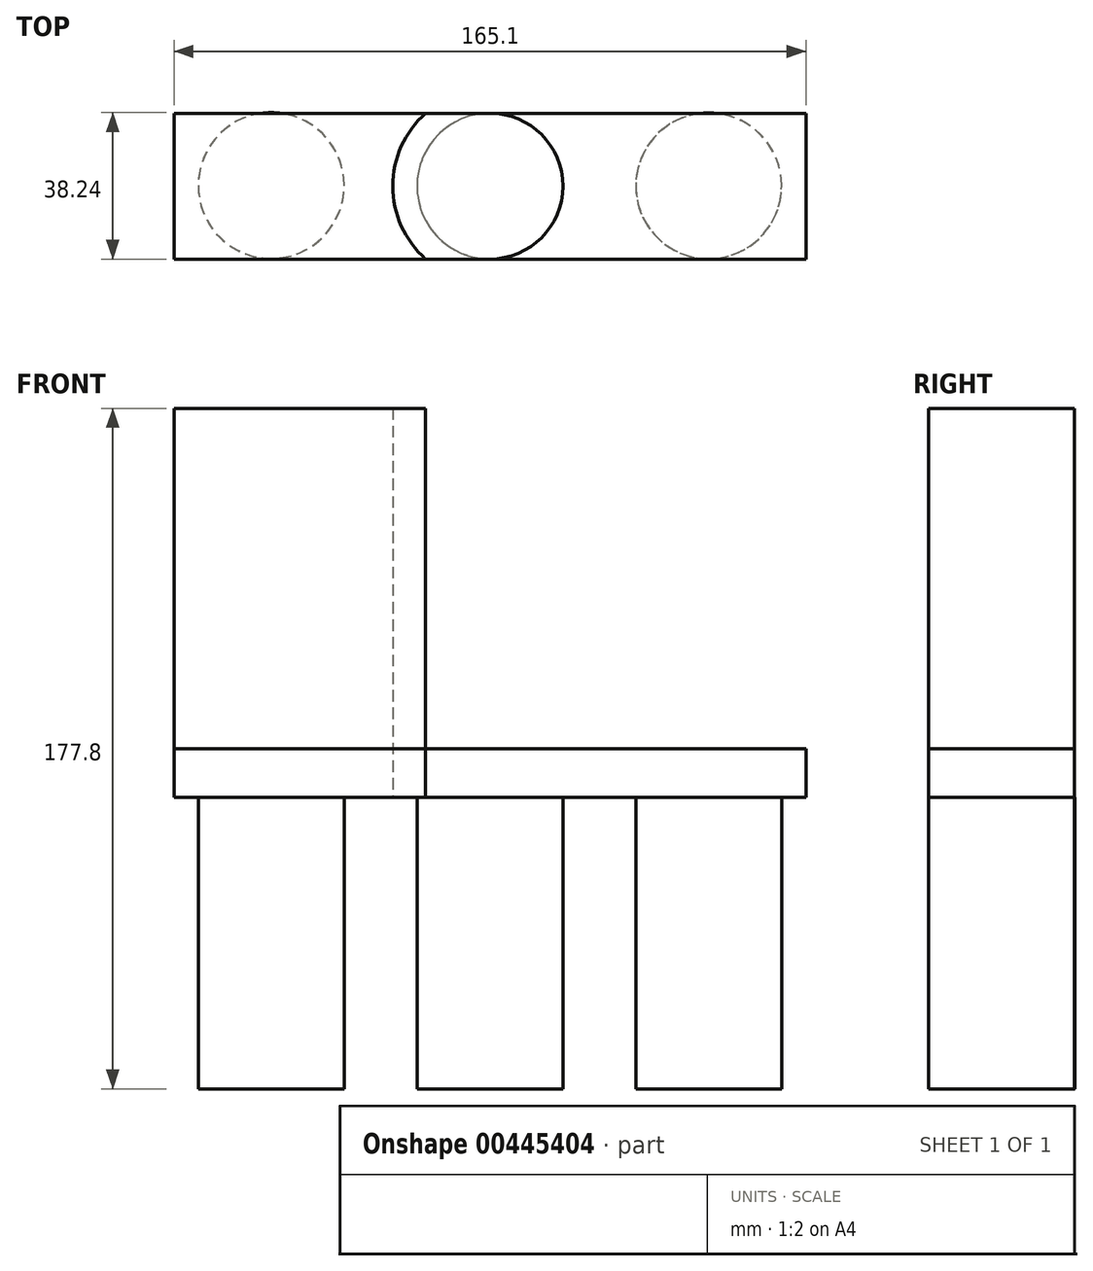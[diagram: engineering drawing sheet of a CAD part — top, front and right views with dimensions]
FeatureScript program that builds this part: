
annotation { "Feature Type Name" : "Feature", "Feature Type Description" : "" }
export const myFeature = defineFeature(function(context is Context, id is Id, definition is map)
    precondition{}
    {
        {
            var Q0;
            Q0=qCreatedBy(makeId("Top.planeOp"),FACE);
            var sketch = newSketch(context, id + "F0", { "sketchPlane" : qUnion([Q0])});
            skLineSegment(sketch, "E0.bottom", {"start": v(82.55, -19.05) * mm, "end": v(-82.55, -19.05) * mm});
            skLineSegment(sketch, "E0.top", {"start": v(82.55, 19.05) * mm, "end": v(-82.55, 19.05) * mm});
            skLineSegment(sketch, "E0.left", {"start": v(82.55, -19.05) * mm, "end": v(82.55, 19.05) * mm});
            skLineSegment(sketch, "E0.right", {"start": v(-82.55, -19.05) * mm, "end": v(-82.55, 19.05) * mm});
            skPoint(sketch, "E0.middle", {"position": v(0, 0) * mm});
            skCircle(sketch, "E1", {"center": v(0, 0) * mm, "radius": 25.4 * mm});
            skSolve(sketch);
        }
        {
            var Q0;
            Q0=makeQuery(id+"F0.imprint","IMPRINT",FACE,{"disambiguationData":[TD([[makeQuery(id+"F0.imprint","IMPRINT",EDGE,{"derivedFrom":sQuery(id+"F0.wireOp",EDGE,"E0.bottom")}),-1.0]])]});
            extrude(context, id + "F1", {"entities" : qUnion([Q0]), "depth" : 12.7 * mm});
        }
        {
            var Q0;
            {var subQ0=sQuery(id+"F0.wireOp",EDGE,"E1");var subQ1=sQuery(id+"F0.wireOp",EDGE,"E0.bottom");var subQ2=makeQuery(id+"F0.imprint","INTERSECT",VERTEX,{"disambiguationData":[OD(0.0)],"derivedFrom":[subQ1,subQ0]});Q0=makeQuery(id+"F0.imprint","IMPRINT",FACE,{"disambiguationData":[TD([[makeQuery(id+"F0.imprint","IMPRINT",EDGE,{"disambiguationData":[TD([[subQ2,-1.0]])],"derivedFrom":subQ1}),-1.0]])]});}
            var Q1;
            {var subQ0=sQuery(id+"F0.wireOp",EDGE,"E1");var subQ1=sQuery(id+"F0.wireOp",EDGE,"E0.top");var subQ2=makeQuery(id+"F0.imprint","INTERSECT",VERTEX,{"disambiguationData":[OD(0.0)],"derivedFrom":[subQ1,subQ0]});Q1=makeQuery(id+"F0.imprint","IMPRINT",FACE,{"disambiguationData":[TD([[makeQuery(id+"F0.imprint","IMPRINT",EDGE,{"disambiguationData":[TD([[subQ2,-1.0]])],"derivedFrom":subQ1}),-1.0]])]});}
            var Q2;
            {var subQ0=sQuery(id+"F0.wireOp",EDGE,"E1");var subQ1=sQuery(id+"F0.wireOp",EDGE,"E0.bottom");var subQ2=makeQuery(id+"F0.imprint","INTERSECT",VERTEX,{"disambiguationData":[OD(0.0)],"derivedFrom":[subQ1,subQ0]});Q2=makeQuery(id+"F0.imprint","IMPRINT",FACE,{"disambiguationData":[TD([[makeQuery(id+"F0.imprint","IMPRINT",EDGE,{"disambiguationData":[TD([[subQ2,-1.0]])],"derivedFrom":subQ1}),1.0]])]});}
            extrude(context, id + "F2", {"entities" : qUnion([Q0, Q1, Q2]), "depth" : 101.6 * mm});
        }
        {
            var Q0;
            Q0=qCreatedBy(makeId("Top.planeOp"),FACE);
            var sketch = newSketch(context, id + "F3", { "sketchPlane" : qUnion([Q0])});
            skCircle(sketch, "E2", {"center": v(0, 0) * mm, "radius": 19.05 * mm});
            skLineSegment(sketch, "E3", {"start": v(0, 0) * mm, "end": v(38.1, 0) * mm});
            skLineSegment(sketch, "E4", {"start": v(0, 0) * mm, "end": v(-38.1, 0) * mm});
            skCircle(sketch, "E5", {"center": v(-57.15, 0.14) * mm, "radius": 19.05 * mm});
            skPoint(sketch, "E5.second.point", {"position": v(-51.83, 18.43) * mm});
            skPoint(sketch, "E5.third.point", {"position": v(-76.2, 0) * mm});
            skCircle(sketch, "E6", {"center": v(57.15, 0.06) * mm, "radius": 19.05 * mm});
            skPoint(sketch, "E6.second.point", {"position": v(76.2, 0) * mm});
            skPoint(sketch, "E6.third.point", {"position": v(60.73, 18.77) * mm});
            skSolve(sketch);
        }
        {
            var Q0;
            Q0=makeQuery(id+"F3.imprint","IMPRINT",FACE,{"disambiguationData":[TD([[makeQuery(id+"F3.imprint","IMPRINT",EDGE,{"derivedFrom":sQuery(id+"F3.wireOp",EDGE,"E5")}),1.0]])]});
            var Q1;
            {var subQ0=sQuery(id+"F3.wireOp",EDGE,"E3");var subQ1=sQuery(id+"F3.wireOp",EDGE,"E2");var subQ2=makeQuery(id+"F3.imprint","INTERSECT",VERTEX,{"derivedFrom":[subQ1,subQ0]});Q1=makeQuery(id+"F3.imprint","IMPRINT",FACE,{"disambiguationData":[TD([[makeQuery(id+"F3.imprint","IMPRINT",EDGE,{"disambiguationData":[TD([[subQ2,1.0]])],"derivedFrom":subQ1}),1.0]])]});}
            var Q2;
            {var subQ0=sQuery(id+"F3.wireOp",EDGE,"E3");var subQ1=sQuery(id+"F3.wireOp",EDGE,"E2");var subQ2=makeQuery(id+"F3.imprint","INTERSECT",VERTEX,{"derivedFrom":[subQ1,subQ0]});Q2=makeQuery(id+"F3.imprint","IMPRINT",FACE,{"disambiguationData":[TD([[makeQuery(id+"F3.imprint","IMPRINT",EDGE,{"disambiguationData":[TD([[subQ2,-1.0]])],"derivedFrom":subQ1}),1.0]])]});}
            var Q3;
            Q3=makeQuery(id+"F3.imprint","IMPRINT",FACE,{"disambiguationData":[TD([[makeQuery(id+"F3.imprint","IMPRINT",EDGE,{"derivedFrom":sQuery(id+"F3.wireOp",EDGE,"E6")}),1.0]])]});
            extrude(context, id + "F4", {"entities" : qUnion([Q0, Q1, Q2, Q3]), "depth" : 0 * mm, "hasSecondDirection" : true, "secondDirectionOppositeDirection" : true, "secondDirectionDepth" : 76.2 * mm});
        }
    });
